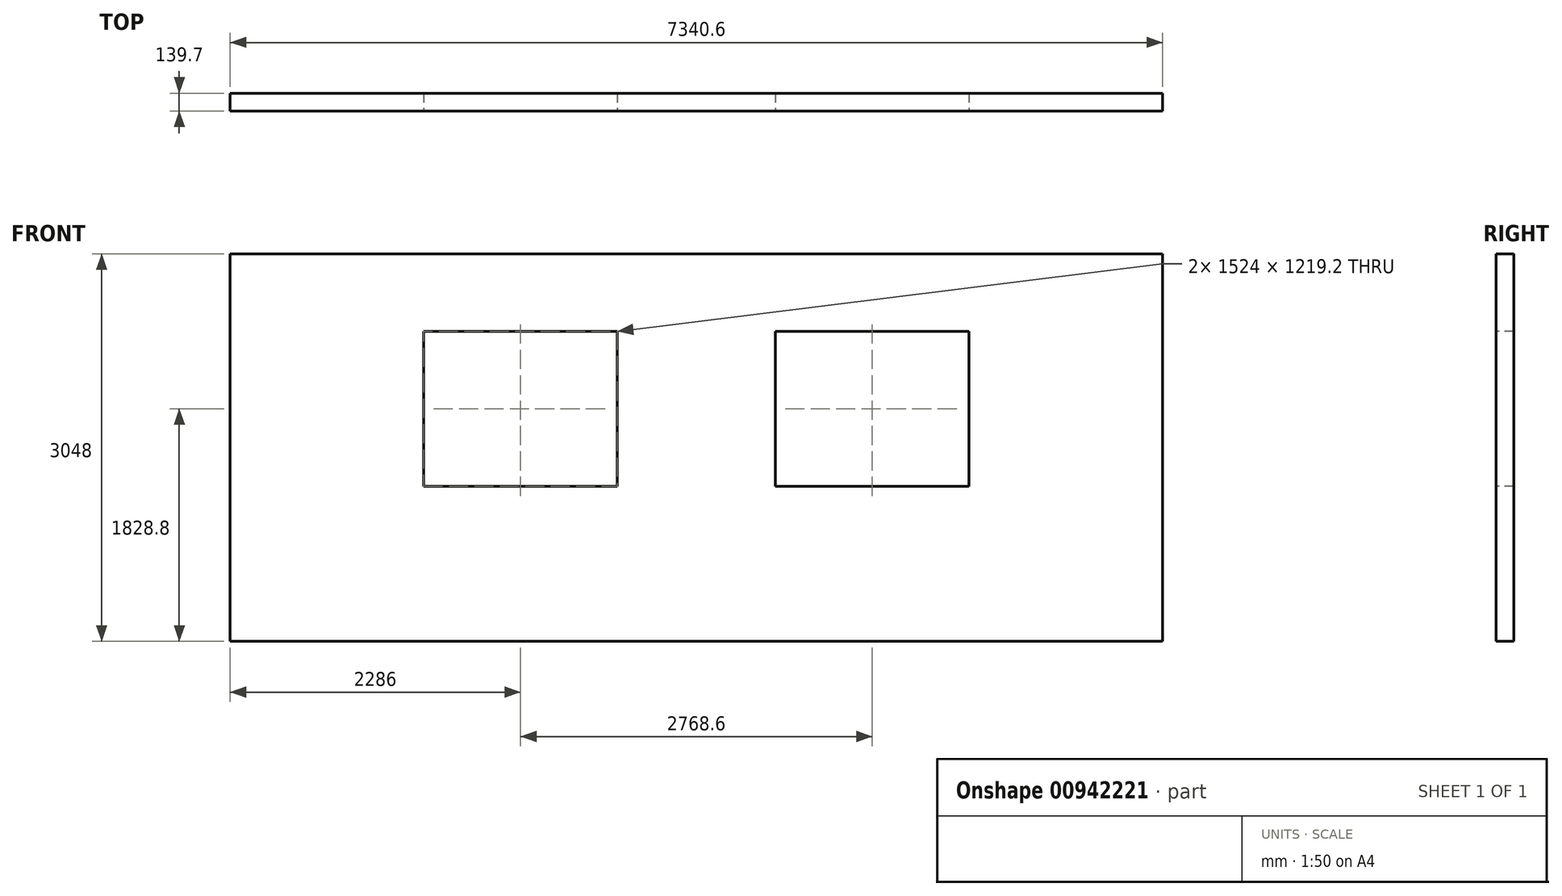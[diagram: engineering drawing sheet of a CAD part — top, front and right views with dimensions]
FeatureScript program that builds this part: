
annotation { "Feature Type Name" : "Feature", "Feature Type Description" : "" }
export const myFeature = defineFeature(function(context is Context, id is Id, definition is map)
    precondition{}
    {
        {
            var Q0;
            Q0=qCreatedBy(makeId("Front.planeOp"),FACE);
            var sketch = newSketch(context, id + "F0", { "sketchPlane" : qUnion([Q0])});
            skLineSegment(sketch, "E0.bottom", {"start": v(0, 0) * mm, "end": v(7340.6, 0) * mm});
            skLineSegment(sketch, "E0.top", {"start": v(0, 3048) * mm, "end": v(7340.6, 3048) * mm});
            skLineSegment(sketch, "E0.left", {"start": v(0, 0) * mm, "end": v(0, 3048) * mm});
            skLineSegment(sketch, "E0.right", {"start": v(7340.6, 0) * mm, "end": v(7340.6, 3048) * mm});
            skLineSegment(sketch, "E1.bottom", {"start": v(1524, 2438.4) * mm, "end": v(3048, 2438.4) * mm});
            skLineSegment(sketch, "E1.top", {"start": v(1524, 1219.2) * mm, "end": v(3048, 1219.2) * mm});
            skLineSegment(sketch, "E1.left", {"start": v(1524, 2438.4) * mm, "end": v(1524, 1219.2) * mm});
            skLineSegment(sketch, "E1.right", {"start": v(3048, 2438.4) * mm, "end": v(3048, 1219.2) * mm});
            skLineSegment(sketch, "E2.bottom", {"start": v(4292.6, 1219.2) * mm, "end": v(5816.6, 1219.2) * mm});
            skLineSegment(sketch, "E2.top", {"start": v(4292.6, 2438.4) * mm, "end": v(5816.6, 2438.4) * mm});
            skLineSegment(sketch, "E2.left", {"start": v(4292.6, 1219.2) * mm, "end": v(4292.6, 2438.4) * mm});
            skLineSegment(sketch, "E2.right", {"start": v(5816.6, 1219.2) * mm, "end": v(5816.6, 2438.4) * mm});
            skSolve(sketch);
        }
        {
            var Q0;
            Q0=makeQuery(id+"F0.imprint","IMPRINT",FACE,{"disambiguationData":[TD([[makeQuery(id+"F0.imprint","IMPRINT",EDGE,{"derivedFrom":sQuery(id+"F0.wireOp",EDGE,"E0.bottom")}),1.0]])]});
            extrude(context, id + "F1", {"entities" : qUnion([Q0]), "oppositeDirection" : true, "depth" : 139.7 * mm, "offsetDistance" : 25.4 * mm});
        }
    });
